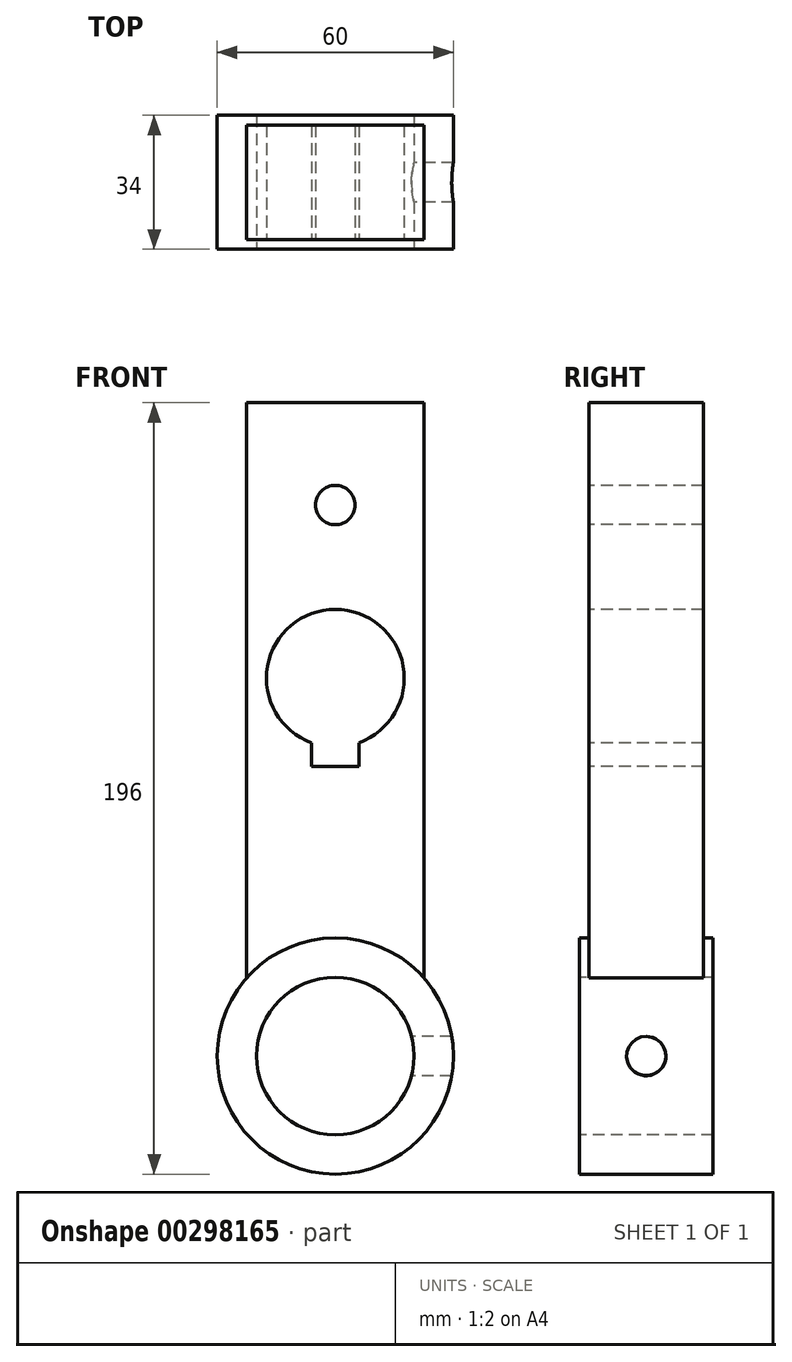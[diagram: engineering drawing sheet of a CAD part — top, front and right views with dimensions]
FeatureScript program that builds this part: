
annotation { "Feature Type Name" : "Feature", "Feature Type Description" : "" }
export const myFeature = defineFeature(function(context is Context, id is Id, definition is map)
    precondition{}
    {
        {
            var Q0;
            Q0=qCreatedBy(makeId("Front.planeOp"),FACE);
            var sketch = newSketch(context, id + "F0", { "sketchPlane" : qUnion([Q0])});
            skCircle(sketch, "E0", {"center": v(0, 0) * mm, "radius": 20 * mm});
            skCircle(sketch, "E1", {"center": v(0, 0) * mm, "radius": 30 * mm});
            skLineSegment(sketch, "E2", {"start": v(-22.5, 19.84) * mm, "end": v(-22.5, 166) * mm});
            skLineSegment(sketch, "E3", {"start": v(-22.5, 166) * mm, "end": v(22.5, 166) * mm});
            skLineSegment(sketch, "E4", {"start": v(22.5, 166) * mm, "end": v(22.5, 19.84) * mm});
            skCircle(sketch, "E5", {"center": v(0, 96) * mm, "radius": 17.5 * mm});
            skLineSegment(sketch, "E6.bottom", {"start": v(6, 73.6) * mm, "end": v(-6, 73.6) * mm});
            skLineSegment(sketch, "E6.left", {"start": v(6, 73.6) * mm, "end": v(6, 83.4) * mm});
            skLineSegment(sketch, "E6.right", {"start": v(-6, 73.6) * mm, "end": v(-6, 83.4) * mm});
            skPoint(sketch, "E6.middle", {"position": v(0, 78.5) * mm});
            skCircle(sketch, "E7", {"center": v(0, 140) * mm, "radius": 5 * mm});
            skArc(sketch, "E8", {"start": v(14, 140) * mm, "mid": v(0, 154) * mm, "end": v(-14, 140) * mm});
            skCircle(sketch, "E9", {"center": v(0, 96) * mm, "radius": 35.4 * mm, "construction": true});
            skSolve(sketch);
        }
        {
            var Q0;
            Q0=makeQuery(id+"F0.imprint","IMPRINT",FACE,{"disambiguationData":[TD([[makeQuery(id+"F0.imprint","IMPRINT",EDGE,{"derivedFrom":sQuery(id+"F0.wireOp",EDGE,"E0")}),-1.0]])]});
            extrude(context, id + "F1", {"entities" : qUnion([Q0]), "endBound" : BoundingType.SYMMETRIC, "oppositeDirection" : true, "depth" : 34 * mm});
        }
        {
            var Q0;
            Q0=qCreatedBy(makeId("Right.planeOp"),FACE);
            var sketch = newSketch(context, id + "F2", { "sketchPlane" : qUnion([Q0])});
            skCircle(sketch, "E10", {"center": v(0, 0) * mm, "radius": 5 * mm});
            skSolve(sketch);
        }
        {
            var Q0;
            Q0 = qSketchRegion(id + "F2", true);
            extrude(context, id + "F3", {"entities" : qUnion([Q0]), "operationType" : NewBodyOperationType.REMOVE, "endBound" : BoundingType.THROUGH_ALL, "depth" : 25 * mm});
        }
        {
            var Q0;
            {var subQ5=sQuery(id+"F0.wireOp",EDGE,"E6.top");Q0=makeQuery(id+"F0.imprint","IMPRINT",FACE,{"disambiguationData":[TD([[makeQuery(id+"F0.imprint","IMPRINT",EDGE,{"derivedFrom":subQ5}),-1.0]])]});}
            var Q1;
            {var subQ5=sQuery(id+"F0.wireOp",EDGE,"E6.bottom");Q1=makeQuery(id+"F0.imprint","IMPRINT",FACE,{"disambiguationData":[TD([[makeQuery(id+"F0.imprint","IMPRINT",EDGE,{"derivedFrom":subQ5}),-1.0]])]});}
            var Q2;
            {var subQ5=sQuery(id+"F0.wireOp",EDGE,"E6.top");Q2=makeQuery(id+"F0.imprint","IMPRINT",FACE,{"disambiguationData":[TD([[makeQuery(id+"F0.imprint","IMPRINT",EDGE,{"derivedFrom":subQ5}),1.0]])]});}
            extrude(context, id + "F4", {"entities" : qUnion([Q0, Q1, Q2]), "operationType" : NewBodyOperationType.REMOVE, "endBound" : BoundingType.SYMMETRIC, "oppositeDirection" : true, "depth" : 25 * mm, "hasSecondDirection" : true, "secondDirectionBound" : SecondDirectionBoundingType.THROUGH_ALL, "secondDirectionOppositeDirection" : false, "secondDirectionDepth" : 25 * mm});
        }
        {
            var Q0;
            {var subQ8=sQuery(id+"F0.wireOp",EDGE,"E6.bottom");Q0=makeQuery(id+"F0.imprint","IMPRINT",FACE,{"disambiguationData":[TD([[makeQuery(id+"F0.imprint","IMPRINT",EDGE,{"derivedFrom":subQ8}),1.0]])]});}
            extrude(context, id + "F5", {"entities" : qUnion([Q0]), "operationType" : NewBodyOperationType.ADD, "endBound" : BoundingType.SYMMETRIC, "oppositeDirection" : true, "depth" : 29 * mm, "hasSecondDirection" : true, "secondDirectionOppositeDirection" : true, "secondDirectionDepth" : 5 * mm});
        }
    });
